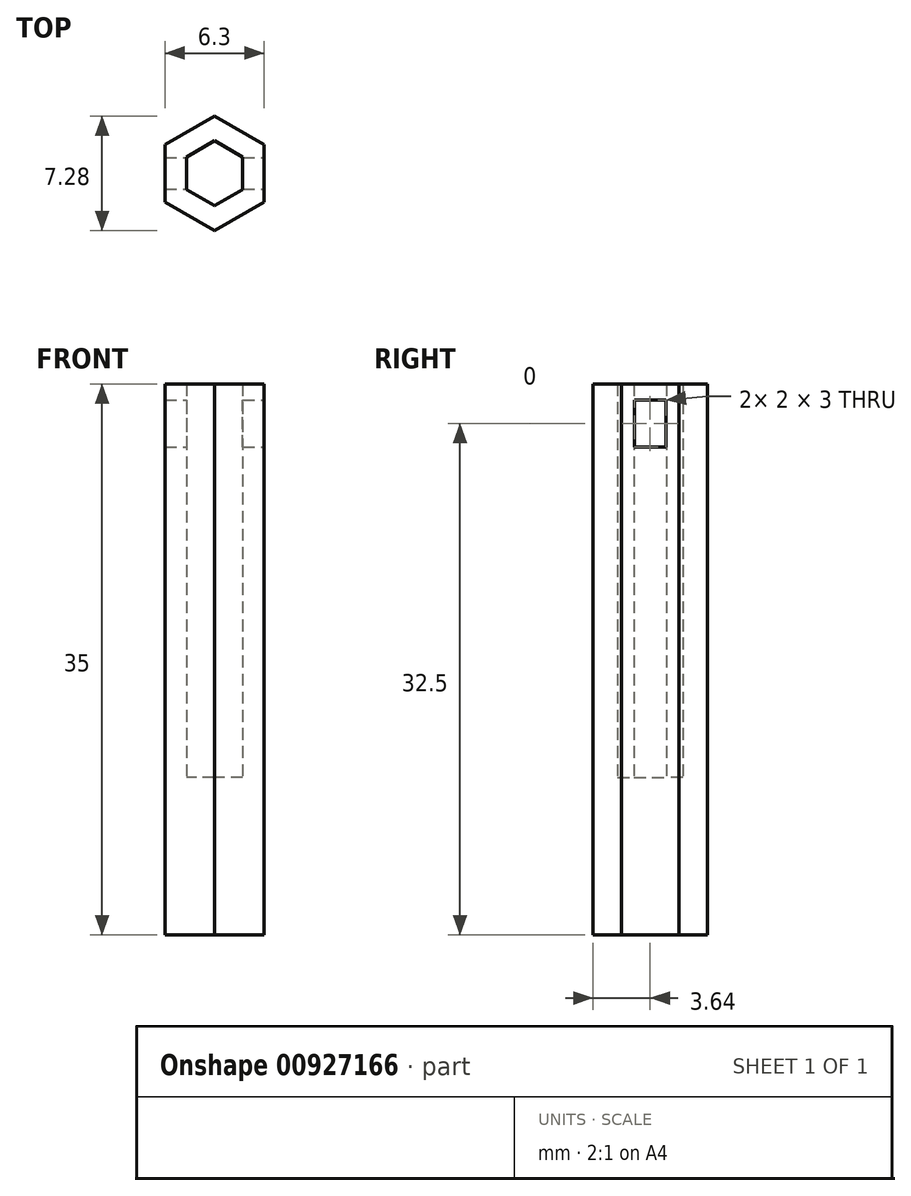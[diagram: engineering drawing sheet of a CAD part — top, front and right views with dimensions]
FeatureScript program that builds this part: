
annotation { "Feature Type Name" : "Feature", "Feature Type Description" : "" }
export const myFeature = defineFeature(function(context is Context, id is Id, definition is map)
    precondition{}
    {
        {
            var Q0;
            Q0=qCreatedBy(makeId("Top.planeOp"),FACE);
            var sketch = newSketch(context, id + "F0", { "sketchPlane" : qUnion([Q0])});
            skCircle(sketch, "E0.cCircle", {"center": v(0, 0) * mm, "radius": 3.15 * mm, "construction": true});
            skLineSegment(sketch, "E0.0", {"start": v(-3.15, -1.82) * mm, "end": v(-3.15, 1.82) * mm});
            skLineSegment(sketch, "E0.1", {"start": v(-3.15, 1.82) * mm, "end": v(0, 3.64) * mm});
            skLineSegment(sketch, "E0.2", {"start": v(0, 3.64) * mm, "end": v(3.15, 1.82) * mm});
            skLineSegment(sketch, "E0.3", {"start": v(3.15, 1.82) * mm, "end": v(3.15, -1.82) * mm});
            skLineSegment(sketch, "E0.4", {"start": v(3.15, -1.82) * mm, "end": v(0, -3.64) * mm});
            skLineSegment(sketch, "E0.5", {"start": v(0, -3.64) * mm, "end": v(-3.15, -1.82) * mm});
            skPoint(sketch, "E0.0.midPoint", {"position": v(-3.15, 0) * mm});
            skSolve(sketch);
        }
        {
            var Q0;
            Q0 = qSketchRegion(id + "F0", true);
            extrude(context, id + "F1", {"entities" : qUnion([Q0]), "depth" : 25 * mm, "offsetDistance" : 25 * mm, "hasSecondDirection" : true, "secondDirectionOppositeDirection" : true, "secondDirectionDepth" : 10 * mm});
        }
        {
            var Q0;
            Q0=qCreatedBy(makeId("Top.planeOp"),FACE);
            var sketch = newSketch(context, id + "F2", { "sketchPlane" : qUnion([Q0])});
            skCircle(sketch, "E1.cCircle", {"center": v(0, 0) * mm, "radius": 1.8 * mm, "construction": true});
            skLineSegment(sketch, "E1.0", {"start": v(-1.8, -1.03) * mm, "end": v(-1.8, 1.03) * mm});
            skLineSegment(sketch, "E1.1", {"start": v(-1.8, 1.03) * mm, "end": v(0, 2.07) * mm});
            skLineSegment(sketch, "E1.2", {"start": v(0, 2.07) * mm, "end": v(1.8, 1.03) * mm});
            skLineSegment(sketch, "E1.3", {"start": v(1.79, 1.03) * mm, "end": v(1.8, -1.03) * mm});
            skLineSegment(sketch, "E1.4", {"start": v(1.8, -1.03) * mm, "end": v(0, -2.07) * mm});
            skLineSegment(sketch, "E1.5", {"start": v(0, -2.07) * mm, "end": v(-1.8, -1.03) * mm});
            skPoint(sketch, "E1.0.midPoint", {"position": v(-1.8, 0) * mm});
            skSolve(sketch);
        }
        {
            var Q0;
            Q0 = qSketchRegion(id + "F2", true);
            extrude(context, id + "F3", {"entities" : qUnion([Q0]), "operationType" : NewBodyOperationType.REMOVE, "depth" : 25 * mm, "offsetDistance" : 25 * mm});
        }
        {
            var Q0;
            Q0=qCreatedBy(makeId("Right.planeOp"),FACE);
            var sketch = newSketch(context, id + "F4", { "sketchPlane" : qUnion([Q0])});
            skLineSegment(sketch, "E2", {"start": v(0, 21) * mm, "end": v(1, 21) * mm});
            skLineSegment(sketch, "E3", {"start": v(1, 21) * mm, "end": v(1, 24) * mm});
            skLineSegment(sketch, "E4", {"start": v(1, 24) * mm, "end": v(0, 24) * mm});
            skLineSegment(sketch, "E5.MirrorCS", {"start": v(-1, 24) * mm, "end": v(0, 24) * mm});
            skLineSegment(sketch, "E6.MirrorCS", {"start": v(-1, 21) * mm, "end": v(-1, 24) * mm});
            skLineSegment(sketch, "E7.MirrorCS", {"start": v(0, 21) * mm, "end": v(-1, 21) * mm});
            skSolve(sketch);
        }
        {
            var Q0;
            Q0 = qSketchRegion(id + "F4", true);
            extrude(context, id + "F5", {"entities" : qUnion([Q0]), "operationType" : NewBodyOperationType.REMOVE, "oppositeDirection" : true, "depth" : 13.6 * mm, "offsetDistance" : 25 * mm, "hasSecondDirection" : true, "secondDirectionOppositeDirection" : false, "secondDirectionDepth" : 25 * mm});
        }
    });
